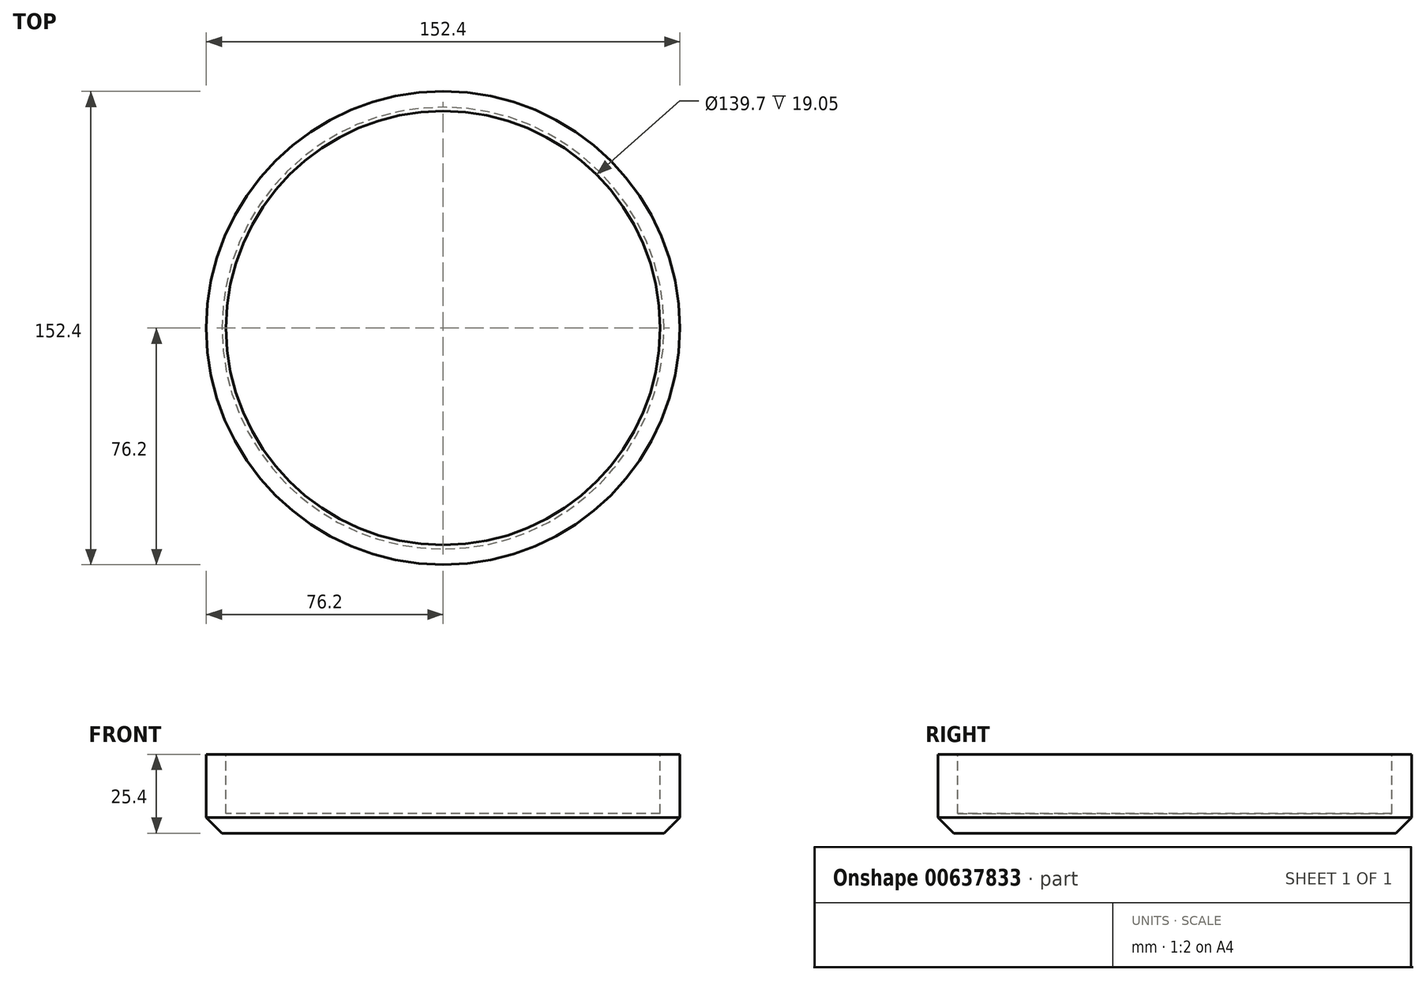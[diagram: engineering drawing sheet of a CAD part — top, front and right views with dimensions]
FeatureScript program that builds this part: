
annotation { "Feature Type Name" : "Feature", "Feature Type Description" : "" }
export const myFeature = defineFeature(function(context is Context, id is Id, definition is map)
    precondition{}
    {
        {
            var Q0;
            Q0=qCreatedBy(makeId("Top.planeOp"),FACE);
            var sketch = newSketch(context, id + "F0", { "sketchPlane" : qUnion([Q0])});
            skCircle(sketch, "E0", {"center": v(0, 0) * mm, "radius": 76.2 * mm});
            skSolve(sketch);
        }
        {
            var Q0;
            Q0 = qSketchRegion(id + "F0", true);
            extrude(context, id + "F1", {"entities" : qUnion([Q0]), "depth" : 25.4 * mm, "offsetDistance" : 25.4 * mm});
        }
        {
            var Q0;
            Q0=makeQuery(id+"F1.opExtrude","CAP_EDGE",EDGE,{"disambiguationData":[OSD([sQuery(id+"F0.wireOp",EDGE,"E0")])],"isStart":true});
            chamfer(context, id + "F2", {"entities" : qUnion([Q0]), "width" : 5.08 * mm, "tangentPropagation" : true});
        }
        {
            var Q0;
            Q0=makeQuery(id+"F1.opExtrude","CAP_FACE",FACE,{"disambiguationData":[OSD([sQuery(id+"F0.wireOp",EDGE,"E0")])],"isStart":false});
            var sketch = newSketch(context, id + "F3", { "sketchPlane" : qUnion([Q0])});
            skPoint(sketch, "E1", {"position": v(0, 0) * mm});
            skSolve(sketch);
        }
        {
            var Q0;
            Q0=sQuery(id+"F3.wireOp",VERTEX,"E1");
            var Q1;
            Q1=makeQuery(id+"F1.opExtrude","SWEPT_BODY",BODY,{"disambiguationData":[OSD([sQuery(id+"F0.wireOp",EDGE,"E0")])]});
            hole(context, id + "F4", {"style" : HoleStyle.SIMPLE, "endStyle" : HoleEndStyle.THROUGH, "holeDiameter" : 139.7 * mm, "majorDiameter" : 6.35 * mm, "isTappedThrough" : true, "tappedDepth" : 12.7 * mm, "tapClearance" : 3, "locations" : qUnion([Q0]), "scope" : qUnion([Q1])});
        }
        {
            var Q0;
            Q0=qCreatedBy(makeId("Top.planeOp"),FACE);
            var sketch = newSketch(context, id + "F5", { "sketchPlane" : qUnion([Q0])});
            skCircle(sketch, "E2", {"center": v(0, 0) * mm, "radius": 69.85 * mm});
            skSolve(sketch);
        }
        {
            var Q0;
            Q0 = qSketchRegion(id + "F5", true);
            extrude(context, id + "F6", {"entities" : qUnion([Q0]), "operationType" : NewBodyOperationType.ADD, "depth" : 6.35 * mm, "offsetDistance" : 25.4 * mm});
        }
    });
